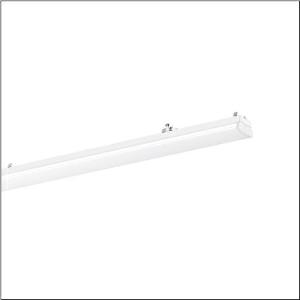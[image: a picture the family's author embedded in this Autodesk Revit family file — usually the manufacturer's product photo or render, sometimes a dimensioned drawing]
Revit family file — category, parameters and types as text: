
# Revit family: licross_r__11_recessed_opal_mo_51tl1ddv44xg_44fd
name_source: partatom
category: Lighting Fixtures
units: mm (PartAtom-declared; Revit-internal decimal feet)

## family parameters
Cut with Voids When Loaded = No
Host = Face
Light Source = No
Part Type = Normal
Room Calculation Point = No
Round Connector Dimension = Use Diameter
Shared = No

## types (1)
- --- (1 x LED, 4120 lm, 22.3 W, 4000K)
    Apparent Load = 22 VA
    CIE Flux Codes = 44 73 91 87 100
    Color Rendering = 80
    Color Temperature = 4000K
    Default Elevation = 1800 mm
    Description = Licross® 11 recessed opal MO, luminaire insert, of sheet steel, coil coated, white, length: 2.250mm, width: 76mm, height: 87mm, LED rated luminous flux: 4.120lm, light colour: 840, control gear: DALI 2, with plug, 5-pole, with phase selection, mains connection: 220..240V, AC, 50/60Hz, rated input power: 22W, halogen-free wiring, primary optical cover: cover, of PMMA, light emission: direct with ceiling illumination distribution, primary light characteristic: symmetric, protection rating (complete): IP40, insulation class (complete): insulation class I (protective earthing), certification: CE, ENEC, VDE, UKCA, protection symbol: D if used in an environment without relevant dust loads with corresponding accessories, impact resistance: IK06, permissible ambient temperature for indoor applications: -25..+45°C, corresponds to IFS (International Featured Standards) requirements for safety and quality in the food industry, reducing of maximum allowable ambient temperature of 5°C with ceiling mounting, LABS conformity tested according to VDMA 24364:2018-05, packaging unit: 1 piece
    Height = 83 mm
    Lamp = 1 x LED
    Lamp Light Flux = 4120 lm
    Lamp Power = 22.3 W
    Lamp count = 1
    Length = 2250 mm
    Luminous efficacy = 185 lm/W
    Manufacturer = Siteco
    ModVariant = No
    Model = 51TL1DDV44XG
    Mounting Place = Ceiling
    Mounting Type = Pendant
    Number of Poles = 1
    OnlyDefault = Yes
    Power Factor = 1
    Product Name = Licross® 11 recessed opal MO
    Product group = luminaire insert
    ProductGroupID = 901
    Protection Class = Protection class I
    Protection Degree = IP 40
    RLX_Detail_Level = 1
    RLX_Emergency_Light_Flux = 0 lm
    RLX_Emergency_Type = 0
    RLX_Emergency_Type_DB = No
    RlxData = <blob elided: 26489 chars, md5=41b098d9>
    Socket = socket
    Standby Power = 0 W
    System Light Flux = 4120 lm
    System Power = 22 W
    Type Comments = factory setting: luminous flux: 100 % | dim-lin: 254 | 100 mA
    Type Image = l_1313666.jpg
    URL = http://relux.com
    VarID = @adj_045531
    Voltage = 0 V
    Weight = 0.00 kg
    Width = 76 mm

## geometry (parser evidence)
native form markers: Blend x4, Sweep x13
no freeform markers — native parametric forms only
